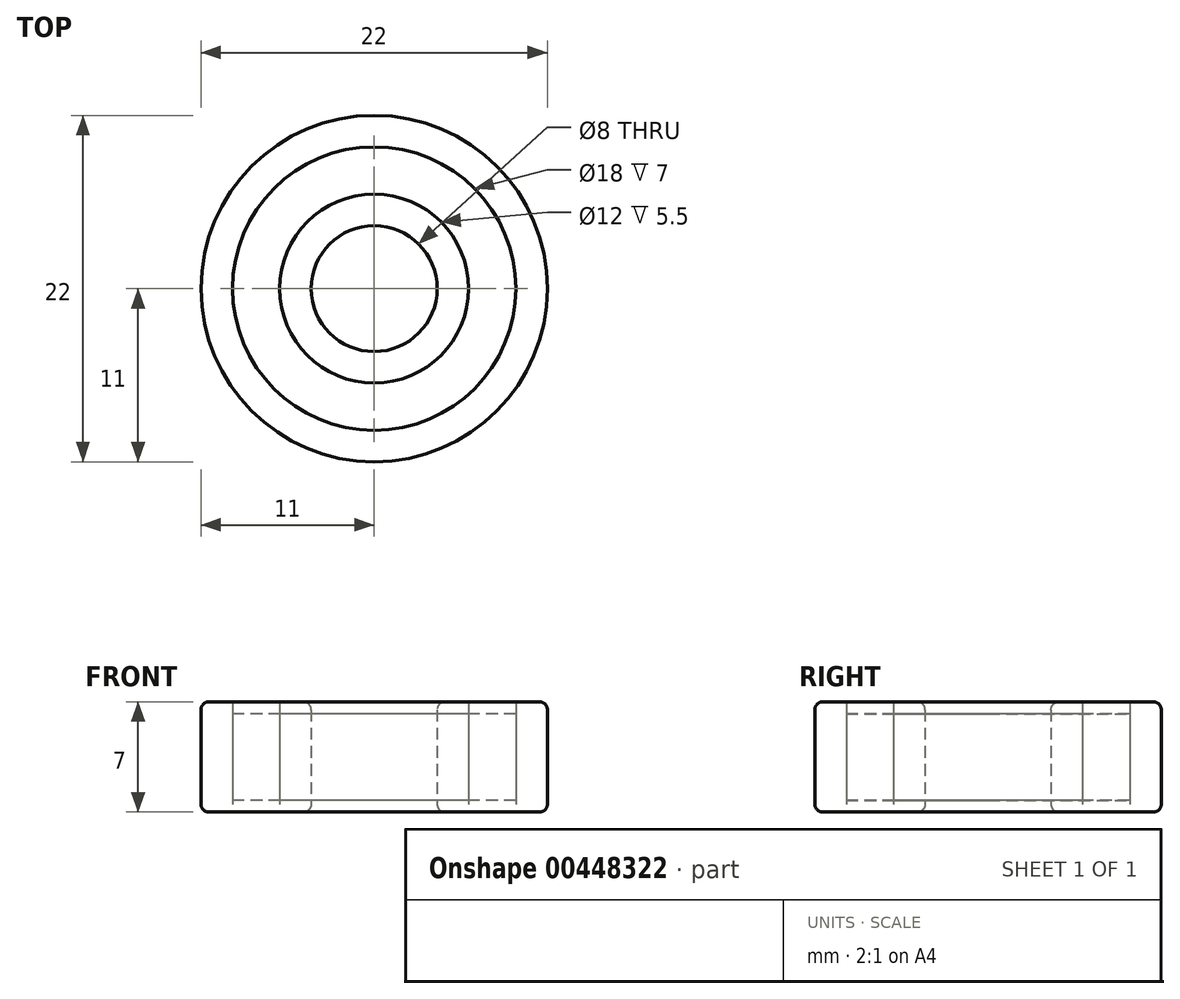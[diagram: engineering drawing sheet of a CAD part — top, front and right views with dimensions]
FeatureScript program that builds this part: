
annotation { "Feature Type Name" : "Feature", "Feature Type Description" : "" }
export const myFeature = defineFeature(function(context is Context, id is Id, definition is map)
    precondition{}
    {
        {
            var Q0;
            Q0=qCreatedBy(makeId("Top.planeOp"),FACE);
            var sketch = newSketch(context, id + "F0", { "sketchPlane" : qUnion([Q0])});
            skCircle(sketch, "E0", {"center": v(0, 0) * mm, "radius": 4 * mm});
            skCircle(sketch, "E1", {"center": v(0, 0) * mm, "radius": 11 * mm});
            skSolve(sketch);
        }
        {
            var Q0;
            Q0=makeQuery(id+"F0.imprint","IMPRINT",FACE,{"disambiguationData":[TD([[makeQuery(id+"F0.imprint","IMPRINT",EDGE,{"derivedFrom":sQuery(id+"F0.wireOp",EDGE,"E0")}),-1.0]])]});
            extrude(context, id + "F1", {"entities" : qUnion([Q0]), "endBound" : BoundingType.SYMMETRIC, "depth" : 7 * mm});
        }
        {
            var Q0;
            Q0=makeQuery(id+"F1.opExtrude","CAP_EDGE",EDGE,{"disambiguationData":[OSD([sQuery(id+"F0.wireOp",EDGE,"E1")])],"isStart":false});
            var Q1;
            Q1=makeQuery(id+"F1.opExtrude","CAP_EDGE",EDGE,{"disambiguationData":[OSD([sQuery(id+"F0.wireOp",EDGE,"E1")])],"isStart":true});
            var Q2;
            Q2=makeQuery(id+"F1.opExtrude","CAP_EDGE",EDGE,{"disambiguationData":[OSD([sQuery(id+"F0.wireOp",EDGE,"E0")])],"isStart":false});
            var Q3;
            Q3=makeQuery(id+"F1.opExtrude","CAP_EDGE",EDGE,{"disambiguationData":[OSD([sQuery(id+"F0.wireOp",EDGE,"E0")])],"isStart":true});
            fillet(context, id + "F2", {"entities" : qUnion([Q0, Q1, Q2, Q3]), "radius" : 0.5 * mm, "tangentPropagation" : true, "allowEdgeOverflow" : false});
        }
        {
            var Q0;
            Q0=qCreatedBy(makeId("Top.planeOp"),FACE);
            var sketch = newSketch(context, id + "F3", { "sketchPlane" : qUnion([Q0])});
            skCircle(sketch, "E2", {"center": v(0, 0) * mm, "radius": 6 * mm});
            skCircle(sketch, "E3", {"center": v(0, 0) * mm, "radius": 9 * mm});
            skSolve(sketch);
        }
        {
            var Q0;
            Q0 = qSketchRegion(id + "F3", true);
            extrude(context, id + "F4", {"entities" : qUnion([Q0]), "operationType" : NewBodyOperationType.REMOVE, "endBound" : BoundingType.SYMMETRIC, "depth" : 11.5 * mm});
        }
        {
            var Q0;
            Q0=qCreatedBy(makeId("Top.planeOp"),FACE);
            var sketch = newSketch(context, id + "F5", { "sketchPlane" : qUnion([Q0])});
            skCircle(sketch, "E4", {"center": v(0, 0) * mm, "radius": 6 * mm});
            skCircle(sketch, "E5", {"center": v(0, 0) * mm, "radius": 9 * mm});
            skSolve(sketch);
        }
        {
            var Q0;
            Q0=makeQuery(id+"F5.imprint","IMPRINT",FACE,{"disambiguationData":[TD([[makeQuery(id+"F5.imprint","IMPRINT",EDGE,{"derivedFrom":sQuery(id+"F5.wireOp",EDGE,"E4")}),-1.0]])]});
            extrude(context, id + "F6", {"entities" : qUnion([Q0]), "endBound" : BoundingType.SYMMETRIC, "depth" : 5.5 * mm});
        }
    });
